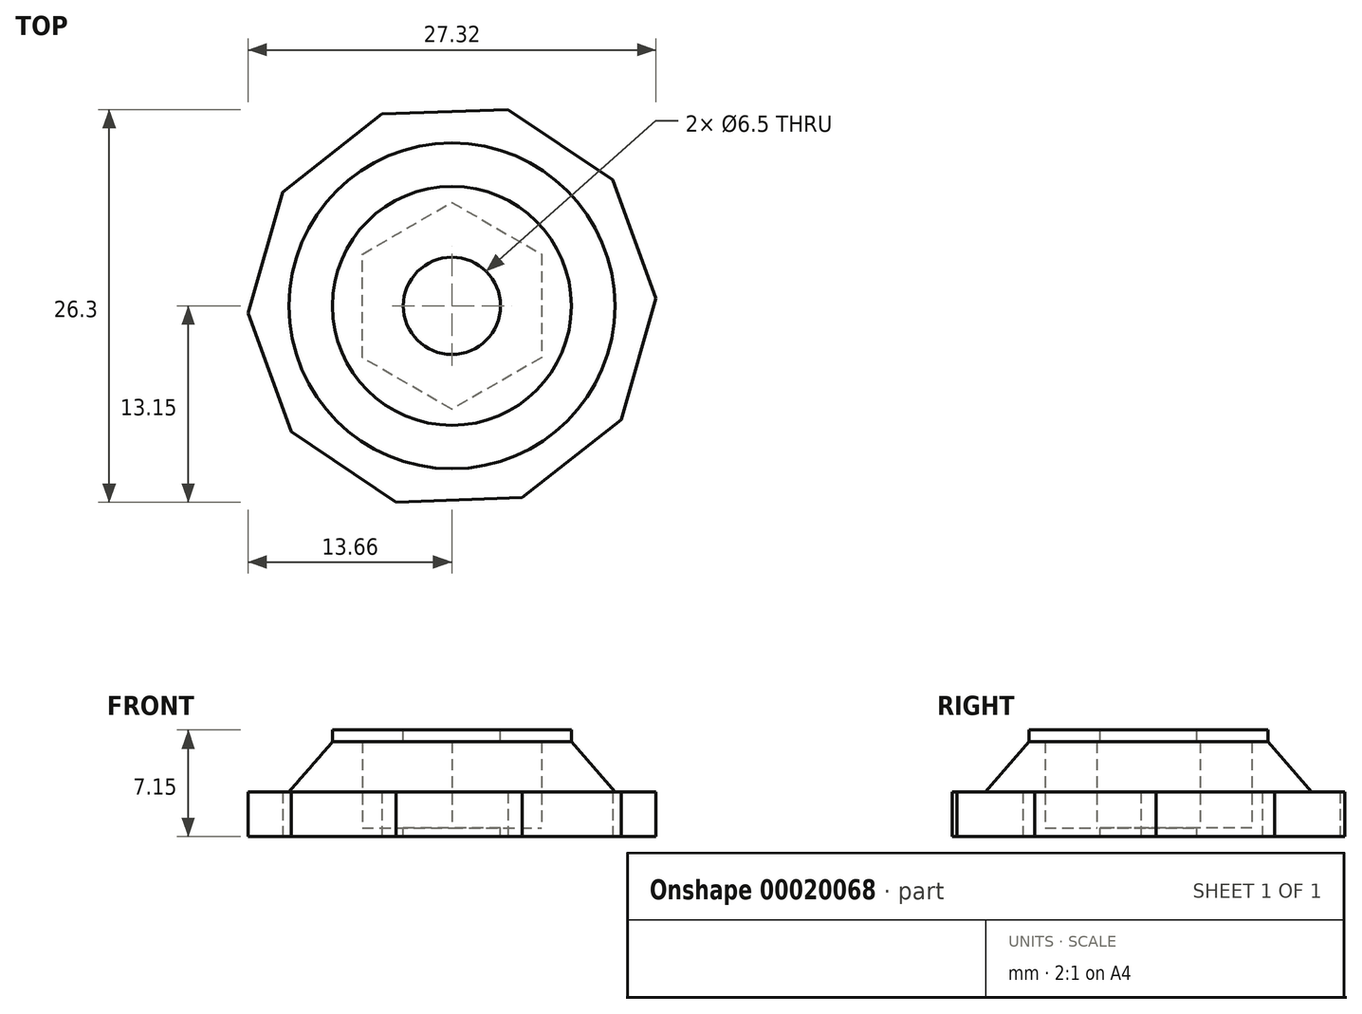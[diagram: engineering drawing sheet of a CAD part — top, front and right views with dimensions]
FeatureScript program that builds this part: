
annotation { "Feature Type Name" : "Feature", "Feature Type Description" : "" }
export const myFeature = defineFeature(function(context is Context, id is Id, definition is map)
    precondition{}
    {
        {
            var Q0;
            Q0=qCreatedBy(makeId("Front.planeOp"),FACE);
            var sketch = newSketch(context, id + "F0", { "sketchPlane" : qUnion([Q0])});
            skLineSegment(sketch, "E0", {"start": v(13, 0) * mm, "end": v(13, 0.6) * mm});
            skLineSegment(sketch, "E1", {"start": v(0, 6.35) * mm, "end": v(0, 7.15) * mm, "construction": true});
            skLineSegment(sketch, "E2", {"start": v(0, 6.35) * mm, "end": v(0, 0.6) * mm, "construction": true});
            skLineSegment(sketch, "E3", {"start": v(8, 7.15) * mm, "end": v(8, 6.35) * mm});
            skLineSegment(sketch, "E4", {"start": v(8, 6.35) * mm, "end": v(13, 0.6) * mm});
            skLineSegment(sketch, "E5", {"start": v(0, 7.15) * mm, "end": v(3.25, 7.15) * mm, "construction": true});
            skLineSegment(sketch, "E6", {"start": v(3.25, 7.15) * mm, "end": v(8, 7.15) * mm});
            skLineSegment(sketch, "E7", {"start": v(3.25, 7.15) * mm, "end": v(3.25, 0) * mm});
            skLineSegment(sketch, "E8", {"start": v(3.25, 0) * mm, "end": v(13, 0) * mm});
            skLineSegment(sketch, "E9", {"start": v(0, 0) * mm, "end": v(13, 0) * mm, "construction": true});
            skLineSegment(sketch, "E10", {"start": v(0, 0.6) * mm, "end": v(0, 0) * mm, "construction": true});
            skSolve(sketch);
        }
        {
            var Q0;
            Q0=makeQuery(id+"F0.imprint","IMPRINT",FACE,{"disambiguationData":[TD([[makeQuery(id+"F0.imprint","IMPRINT",EDGE,{"derivedFrom":sQuery(id+"F0.wireOp",EDGE,"E0")}),1.0]])]});
            var Q1;
            Q1=sQuery(id+"F0.wireOp",EDGE,"E2");
            revolve(context, id + "F1", {"entities" : qUnion([Q0]), "axis" : qUnion([Q1]), "revolveType" : RevolveType.FULL});
        }
        {
            var Q0;
            Q0=makeQuery(id+"F1.opRevolve","SWEPT_FACE",FACE,{"disambiguationData":[OSD([sQuery(id+"F0.wireOp",EDGE,"E8")])]});
            var sketch = newSketch(context, id + "F2", { "sketchPlane" : qUnion([Q0])});
            skCircle(sketch, "E11.cCircle", {"center": v(0, 0) * mm, "radius": 13 * mm, "construction": true});
            skLineSegment(sketch, "E11.0", {"start": v(10.76, -8.43) * mm, "end": v(3.75, -13.15) * mm});
            skLineSegment(sketch, "E11.1", {"start": v(3.75, -13.15) * mm, "end": v(-4.7, -12.84) * mm});
            skLineSegment(sketch, "E11.2", {"start": v(-4.7, -12.84) * mm, "end": v(-11.34, -7.63) * mm});
            skLineSegment(sketch, "E11.3", {"start": v(-11.34, -7.63) * mm, "end": v(-13.66, 0.5) * mm});
            skLineSegment(sketch, "E11.4", {"start": v(-13.66, 0.5) * mm, "end": v(-10.76, 8.43) * mm});
            skLineSegment(sketch, "E11.5", {"start": v(-10.76, 8.43) * mm, "end": v(-3.75, 13.15) * mm});
            skLineSegment(sketch, "E11.6", {"start": v(-3.75, 13.15) * mm, "end": v(4.7, 12.84) * mm});
            skLineSegment(sketch, "E11.7", {"start": v(4.7, 12.84) * mm, "end": v(11.34, 7.63) * mm});
            skLineSegment(sketch, "E11.8", {"start": v(11.34, 7.63) * mm, "end": v(13.66, -0.5) * mm});
            skLineSegment(sketch, "E11.9", {"start": v(13.66, -0.5) * mm, "end": v(10.76, -8.43) * mm});
            skPoint(sketch, "E11.0.midPoint", {"position": v(7.25, -10.79) * mm});
            skLineSegment(sketch, "E12", {"start": v(0, 0) * mm, "end": v(7.25, -10.79) * mm, "construction": true});
            skSolve(sketch);
        }
        {
            var Q0;
            {var subQ1=sQuery(id+"F2.wireOp",EDGE,"E11.6");var subQ3=sQuery(id+"F2.wireOp",EDGE,"E11.5");var subQ5=makeQuery(id+"F2.imprint","INTERSECT",VERTEX,{"derivedFrom":[subQ3,subQ1]});Q0=makeQuery(id+"F2.imprint","IMPRINT",FACE,{"disambiguationData":[TD([[makeQuery(id+"F2.imprint","IMPRINT",EDGE,{"disambiguationData":[TD([[subQ5,1.0]])],"derivedFrom":subQ3}),-1.0]])]});}
            var Q1;
            {var subQ1=sQuery(id+"F2.wireOp",EDGE,"E11.5");var subQ3=sQuery(id+"F2.wireOp",EDGE,"E11.4");var subQ5=makeQuery(id+"F2.imprint","INTERSECT",VERTEX,{"derivedFrom":[subQ3,subQ1]});Q1=makeQuery(id+"F2.imprint","IMPRINT",FACE,{"disambiguationData":[TD([[makeQuery(id+"F2.imprint","IMPRINT",EDGE,{"disambiguationData":[TD([[subQ5,1.0]])],"derivedFrom":subQ3}),-1.0]])]});}
            var Q2;
            {var subQ1=sQuery(id+"F2.wireOp",EDGE,"E11.7");var subQ3=sQuery(id+"F2.wireOp",EDGE,"E11.6");var subQ5=makeQuery(id+"F2.imprint","INTERSECT",VERTEX,{"derivedFrom":[subQ3,subQ1]});Q2=makeQuery(id+"F2.imprint","IMPRINT",FACE,{"disambiguationData":[TD([[makeQuery(id+"F2.imprint","IMPRINT",EDGE,{"disambiguationData":[TD([[subQ5,1.0]])],"derivedFrom":subQ3}),-1.0]])]});}
            var Q3;
            {var subQ1=sQuery(id+"F2.wireOp",EDGE,"E11.8");var subQ3=sQuery(id+"F2.wireOp",EDGE,"E11.7");var subQ5=makeQuery(id+"F2.imprint","INTERSECT",VERTEX,{"derivedFrom":[subQ3,subQ1]});Q3=makeQuery(id+"F2.imprint","IMPRINT",FACE,{"disambiguationData":[TD([[makeQuery(id+"F2.imprint","IMPRINT",EDGE,{"disambiguationData":[TD([[subQ5,1.0]])],"derivedFrom":subQ3}),-1.0]])]});}
            var Q4;
            {var subQ0=sQuery(id+"F2.wireOp",EDGE,"E11.9");var subQ3=sQuery(id+"F2.wireOp",EDGE,"E11.8");var subQ4=makeQuery(id+"F2.imprint","INTERSECT",VERTEX,{"derivedFrom":[subQ3,subQ0]});Q4=makeQuery(id+"F2.imprint","IMPRINT",FACE,{"disambiguationData":[TD([[makeQuery(id+"F2.imprint","IMPRINT",EDGE,{"disambiguationData":[TD([[subQ4,1.0]])],"derivedFrom":subQ3}),-1.0]])]});}
            var Q5;
            {var subQ0=sQuery(id+"F0.wireOp",EDGE,"E8");Q5=makeQuery(id+"F2.imprint","IMPRINT",FACE,{"disambiguationData":[TD([[makeQuery(id+"F2.imprint","IMPRINT",EDGE,{"derivedFrom":makeQuery(id+"F1.opRevolve","SWEPT_EDGE",EDGE,{"disambiguationData":[OSD([sQuery(id+"F0.wireOp",EDGE,"E7"),subQ0])]})}),1.0]])]});}
            var Q6;
            {var subQ1=sQuery(id+"F2.wireOp",EDGE,"E11.9");var subQ3=sQuery(id+"F2.wireOp",EDGE,"E11.0");var subQ5=makeQuery(id+"F2.imprint","INTERSECT",VERTEX,{"derivedFrom":[subQ3,subQ1]});Q6=makeQuery(id+"F2.imprint","IMPRINT",FACE,{"disambiguationData":[TD([[makeQuery(id+"F2.imprint","IMPRINT",EDGE,{"disambiguationData":[TD([[subQ5,-1.0]])],"derivedFrom":subQ3}),-1.0]])]});}
            var Q7;
            {var subQ1=sQuery(id+"F2.wireOp",EDGE,"E11.1");var subQ3=sQuery(id+"F2.wireOp",EDGE,"E11.0");var subQ5=makeQuery(id+"F2.imprint","INTERSECT",VERTEX,{"derivedFrom":[subQ3,subQ1]});Q7=makeQuery(id+"F2.imprint","IMPRINT",FACE,{"disambiguationData":[TD([[makeQuery(id+"F2.imprint","IMPRINT",EDGE,{"disambiguationData":[TD([[subQ5,1.0]])],"derivedFrom":subQ3}),-1.0]])]});}
            var Q8;
            {var subQ1=sQuery(id+"F2.wireOp",EDGE,"E11.2");var subQ3=sQuery(id+"F2.wireOp",EDGE,"E11.1");var subQ5=makeQuery(id+"F2.imprint","INTERSECT",VERTEX,{"derivedFrom":[subQ3,subQ1]});Q8=makeQuery(id+"F2.imprint","IMPRINT",FACE,{"disambiguationData":[TD([[makeQuery(id+"F2.imprint","IMPRINT",EDGE,{"disambiguationData":[TD([[subQ5,1.0]])],"derivedFrom":subQ3}),-1.0]])]});}
            var Q9;
            {var subQ1=sQuery(id+"F2.wireOp",EDGE,"E11.3");var subQ3=sQuery(id+"F2.wireOp",EDGE,"E11.2");var subQ5=makeQuery(id+"F2.imprint","INTERSECT",VERTEX,{"derivedFrom":[subQ3,subQ1]});Q9=makeQuery(id+"F2.imprint","IMPRINT",FACE,{"disambiguationData":[TD([[makeQuery(id+"F2.imprint","IMPRINT",EDGE,{"disambiguationData":[TD([[subQ5,1.0]])],"derivedFrom":subQ3}),-1.0]])]});}
            var Q10;
            {var subQ1=sQuery(id+"F2.wireOp",EDGE,"E11.4");var subQ3=sQuery(id+"F2.wireOp",EDGE,"E11.3");var subQ5=makeQuery(id+"F2.imprint","INTERSECT",VERTEX,{"derivedFrom":[subQ3,subQ1]});Q10=makeQuery(id+"F2.imprint","IMPRINT",FACE,{"disambiguationData":[TD([[makeQuery(id+"F2.imprint","IMPRINT",EDGE,{"disambiguationData":[TD([[subQ5,1.0]])],"derivedFrom":subQ3}),-1.0]])]});}
            extrude(context, id + "F3", {"entities" : qUnion([Q0, Q1, Q2, Q3, Q4, Q5, Q6, Q7, Q8, Q9, Q10]), "operationType" : NewBodyOperationType.ADD, "oppositeDirection" : true, "depth" : 3 * mm});
        }
        {
            var Q0;
            Q0=sQuery(id+"F0.wireOp",VERTEX,"E2.end");
            var Q1;
            Q1=makeQuery(id+"F1.opRevolve","SWEPT_FACE",FACE,{"disambiguationData":[OSD([sQuery(id+"F0.wireOp",EDGE,"E6")])]});
            cPlane(context, id + "F4", {"entities" : qUnion([Q0, Q1]), "cplaneType" : CPlaneType.PLANE_POINT, "offset" : 150 * mm, "width" : 150 * mm, "height" : 150 * mm});
        }
        {
            var Q0;
            Q0=qCreatedBy(id+"F4.planeOp",FACE);
            var sketch = newSketch(context, id + "F5", { "sketchPlane" : qUnion([Q0])});
            skCircle(sketch, "E13.cCircle", {"center": v(0, 0) * mm, "radius": 6 * mm, "construction": true});
            skLineSegment(sketch, "E13.0", {"start": v(6, 3.46) * mm, "end": v(6, -3.46) * mm});
            skLineSegment(sketch, "E13.1", {"start": v(6, -3.46) * mm, "end": v(0, -6.93) * mm});
            skLineSegment(sketch, "E13.2", {"start": v(0, -6.93) * mm, "end": v(-6, -3.46) * mm});
            skLineSegment(sketch, "E13.3", {"start": v(-6, -3.46) * mm, "end": v(-6, 3.46) * mm});
            skLineSegment(sketch, "E13.4", {"start": v(-6, 3.46) * mm, "end": v(0, 6.93) * mm});
            skLineSegment(sketch, "E13.5", {"start": v(0, 6.93) * mm, "end": v(6, 3.46) * mm});
            skPoint(sketch, "E13.0.midPoint", {"position": v(6, 0) * mm});
            skLineSegment(sketch, "E14", {"start": v(0, 0) * mm, "end": v(6, 0) * mm});
            skSolve(sketch);
        }
        {
            var Q0;
            {var subQ1=sQuery(id+"F5.wireOp",EDGE,"E13.1");Q0=makeQuery(id+"F5.imprint","IMPRINT",FACE,{"disambiguationData":[TD([[makeQuery(id+"F5.imprint","IMPRINT",EDGE,{"derivedFrom":subQ1}),-1.0]])]});}
            extrude(context, id + "F6", {"entities" : qUnion([Q0]), "operationType" : NewBodyOperationType.REMOVE, "depth" : 5.75 * mm});
        }
    });
